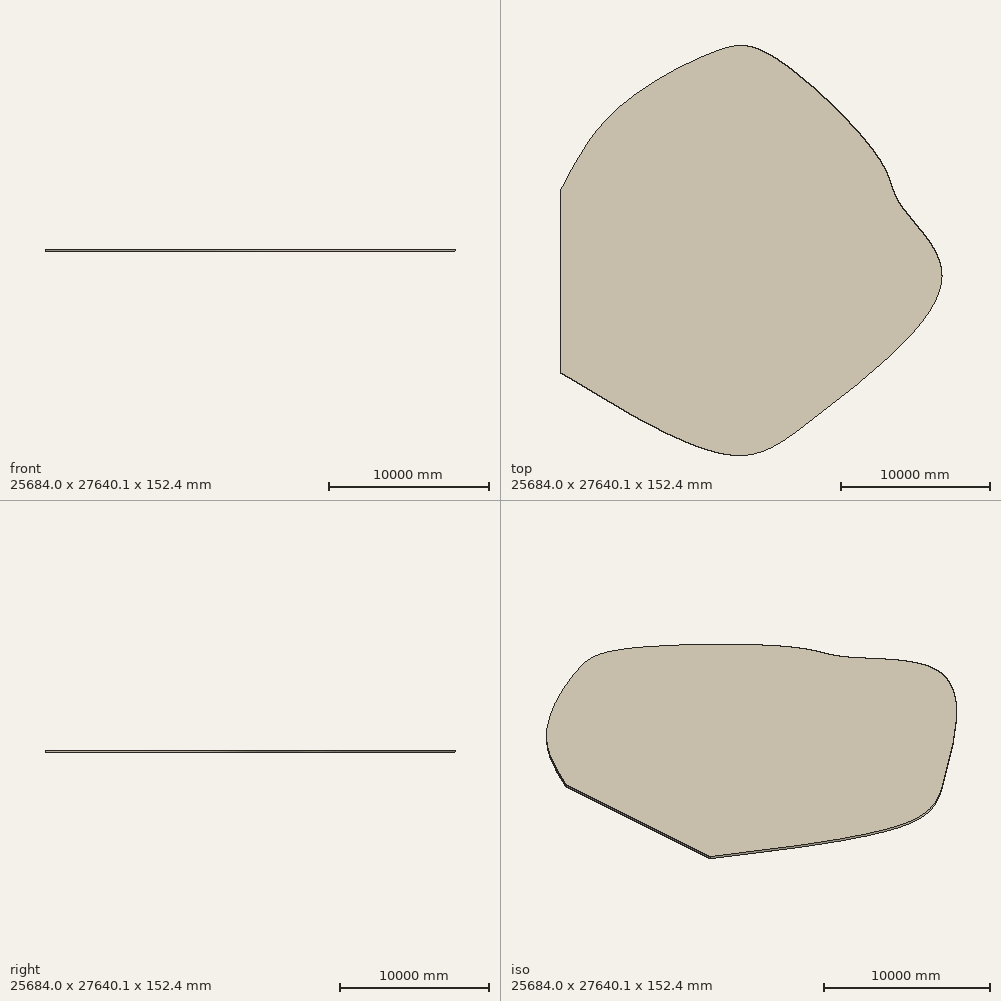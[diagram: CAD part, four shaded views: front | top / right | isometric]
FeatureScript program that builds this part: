
annotation { "Feature Type Name" : "Feature", "Feature Type Description" : "" }
export const myFeature = defineFeature(function(context is Context, id is Id, definition is map)
    precondition{}
    {
        {
            var Q0;
            Q0=qCreatedBy(makeId("Top.planeOp"),FACE);
            var sketch = newSketch(context, id + "F0", { "sketchPlane" : qUnion([Q0])});
            skLineSegment(sketch, "E0.left", {"start": v(-9258.22, -3931.02) * mm, "end": v(-9258.22, 8407.78) * mm});
            skFitSpline(sketch, "E1", {"points": [v(4786.07, -3931.02) * mm, v(9607.88, -2901.59) * mm, v(11915.55, -1788) * mm, v(8020.41, 3363.3) * mm, v(8647.39, 6967.58) * mm, v(1599.53, 11370.9) * mm, v(-9258.22, 8407.78) * mm], "startDerivative": vector(48943.04, -7588.32) * mm, "endDerivative": vector(-46914.73, -23055.23) * mm});
            skLineSegment(sketch, "E2", {"start": v(4786.07, -3931.02) * mm, "end": v(-9258.22, -3931.02) * mm});
            skFitSpline(sketch, "E3", {"points": [v(-9258.22, -3931.02) * mm, v(2490.9, -9488.46) * mm, v(8139.4, -6745.9) * mm, v(16421.03, 2414.98) * mm, v(13591.4, 7465.78) * mm, v(12375.17, 10221.1) * mm, v(4641.87, 17627) * mm, v(1168.73, 17753.9) * mm, v(-5588.3, 13737.48) * mm, v(-9258.22, 8407.78) * mm], "startDerivative": vector(88812.55, -54416.29) * mm, "endDerivative": vector(-27365.5, -53001.7) * mm});
            skSolve(sketch);
        }
        {
            var Q0;
            Q0 = qSketchRegion(id + "F0", true);
            extrude(context, id + "F1", {"entities" : qUnion([Q0]), "depth" : 152.4 * mm});
        }
    });
